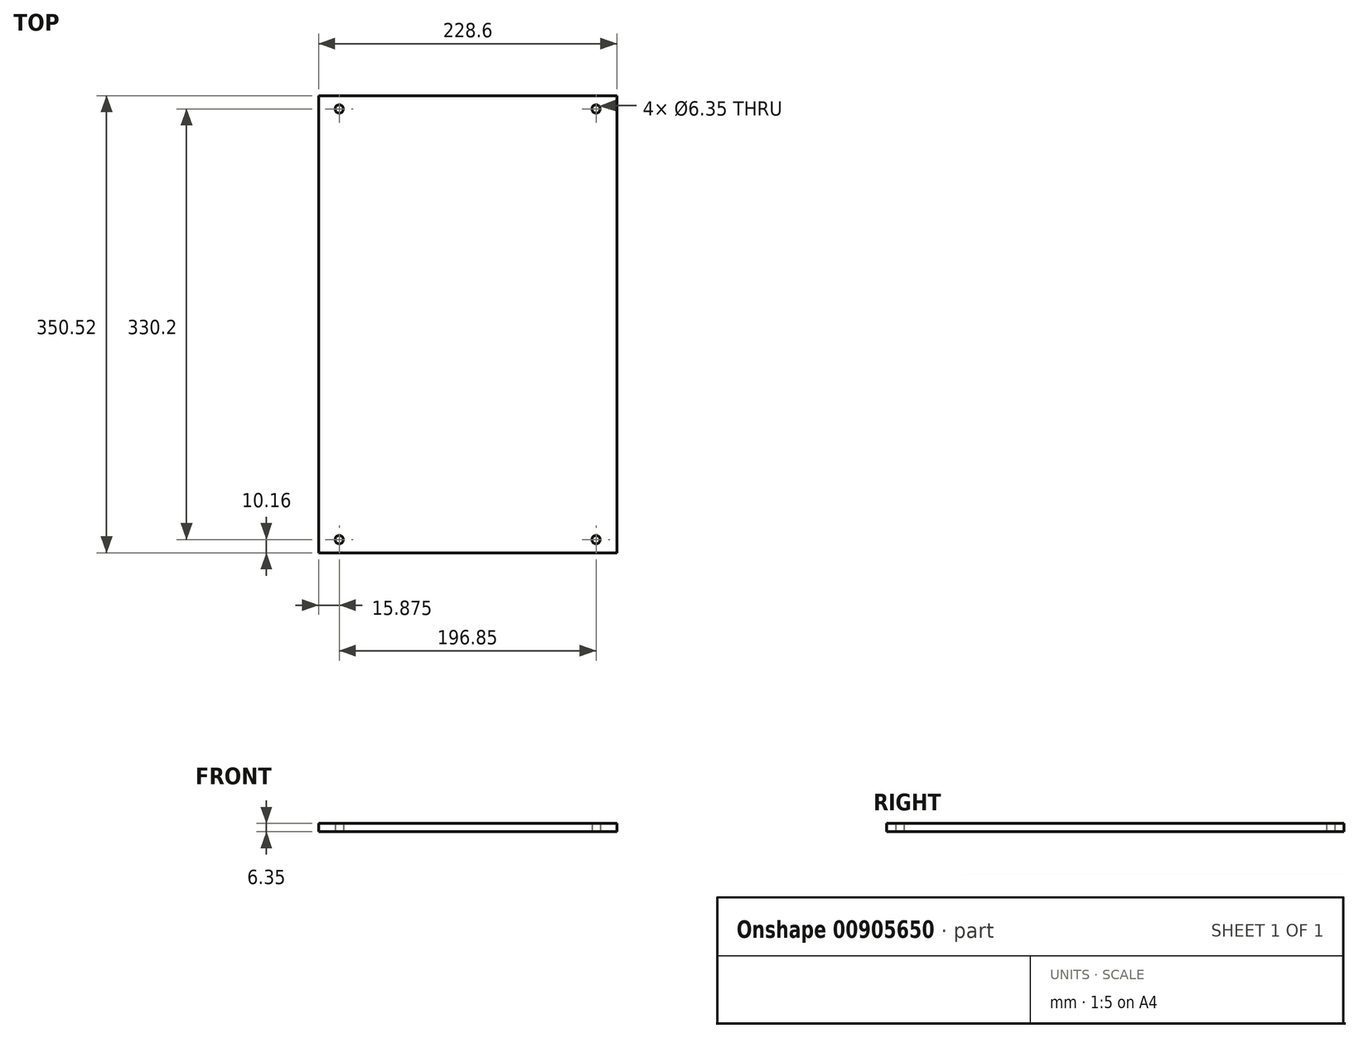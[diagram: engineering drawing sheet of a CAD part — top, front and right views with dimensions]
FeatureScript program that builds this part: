
annotation { "Feature Type Name" : "Feature", "Feature Type Description" : "" }
export const myFeature = defineFeature(function(context is Context, id is Id, definition is map)
    precondition{}
    {
        {
            var Q0;
            Q0=qCreatedBy(makeId("Top.planeOp"),FACE);
            var sketch = newSketch(context, id + "F0", { "sketchPlane" : qUnion([Q0])});
            skLineSegment(sketch, "E0.bottom", {"start": v(-114.3, 175.26) * mm, "end": v(114.3, 175.26) * mm});
            skLineSegment(sketch, "E0.top", {"start": v(-114.3, -175.26) * mm, "end": v(114.3, -175.26) * mm});
            skLineSegment(sketch, "E0.left", {"start": v(-114.3, 175.26) * mm, "end": v(-114.3, -175.26) * mm});
            skLineSegment(sketch, "E0.right", {"start": v(114.3, 175.26) * mm, "end": v(114.3, -175.26) * mm});
            skPoint(sketch, "E0.middle", {"position": v(0, 0) * mm});
            skLineSegment(sketch, "E1.bottom", {"start": v(-98.42, 165.1) * mm, "end": v(98.43, 165.1) * mm, "construction": true});
            skLineSegment(sketch, "E1.top", {"start": v(-98.43, -165.1) * mm, "end": v(98.42, -165.1) * mm, "construction": true});
            skLineSegment(sketch, "E1.left", {"start": v(-98.42, 165.1) * mm, "end": v(-98.43, -165.1) * mm, "construction": true});
            skLineSegment(sketch, "E1.right", {"start": v(98.43, 165.1) * mm, "end": v(98.42, -165.1) * mm, "construction": true});
            skCircle(sketch, "E2", {"center": v(-98.42, 165.1) * mm, "radius": 3.18 * mm});
            skCircle(sketch, "E3", {"center": v(98.43, 165.1) * mm, "radius": 3.18 * mm});
            skCircle(sketch, "E4", {"center": v(-98.43, -165.1) * mm, "radius": 3.18 * mm});
            skCircle(sketch, "E5", {"center": v(98.42, -165.1) * mm, "radius": 3.18 * mm});
            skSolve(sketch);
        }
        {
            var Q0;
            Q0 = qSketchRegion(id + "F0", true);
            extrude(context, id + "F1", {"entities" : qUnion([Q0]), "depth" : 6.35 * mm, "offsetDistance" : 25.4 * mm});
        }
    });
